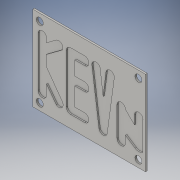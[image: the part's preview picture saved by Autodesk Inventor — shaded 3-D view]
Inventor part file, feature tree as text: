
AUTODESK INVENTOR PART (.ipt)
format: ipt  version: 2016 (Build 200138000, 138)  size: 363,008 bytes
history: native  units: in
note: dims shown in document units (in); Inventor stores cm internally (conversion verified against a paired STEP export)
features: sketch x2, extrude x1, emboss x1
ambient origin geometry x8: Origin, YZ Plane, XZ Plane, XY Plane, X Axis, Y Axis, Z Axis, Center Point
bodies: Solid1 (feature_tree)
feature tree (4):
  extrude  "Extrusion1"  Depth=0.1in TaperAngle=0.0deg
  emboss  "Emboss1"
  sketch  "Sketch1"  dims[d15=0.125in d16=0.0in d42=0.1in d43=0.0in]
  sketch  "Sketch2"
